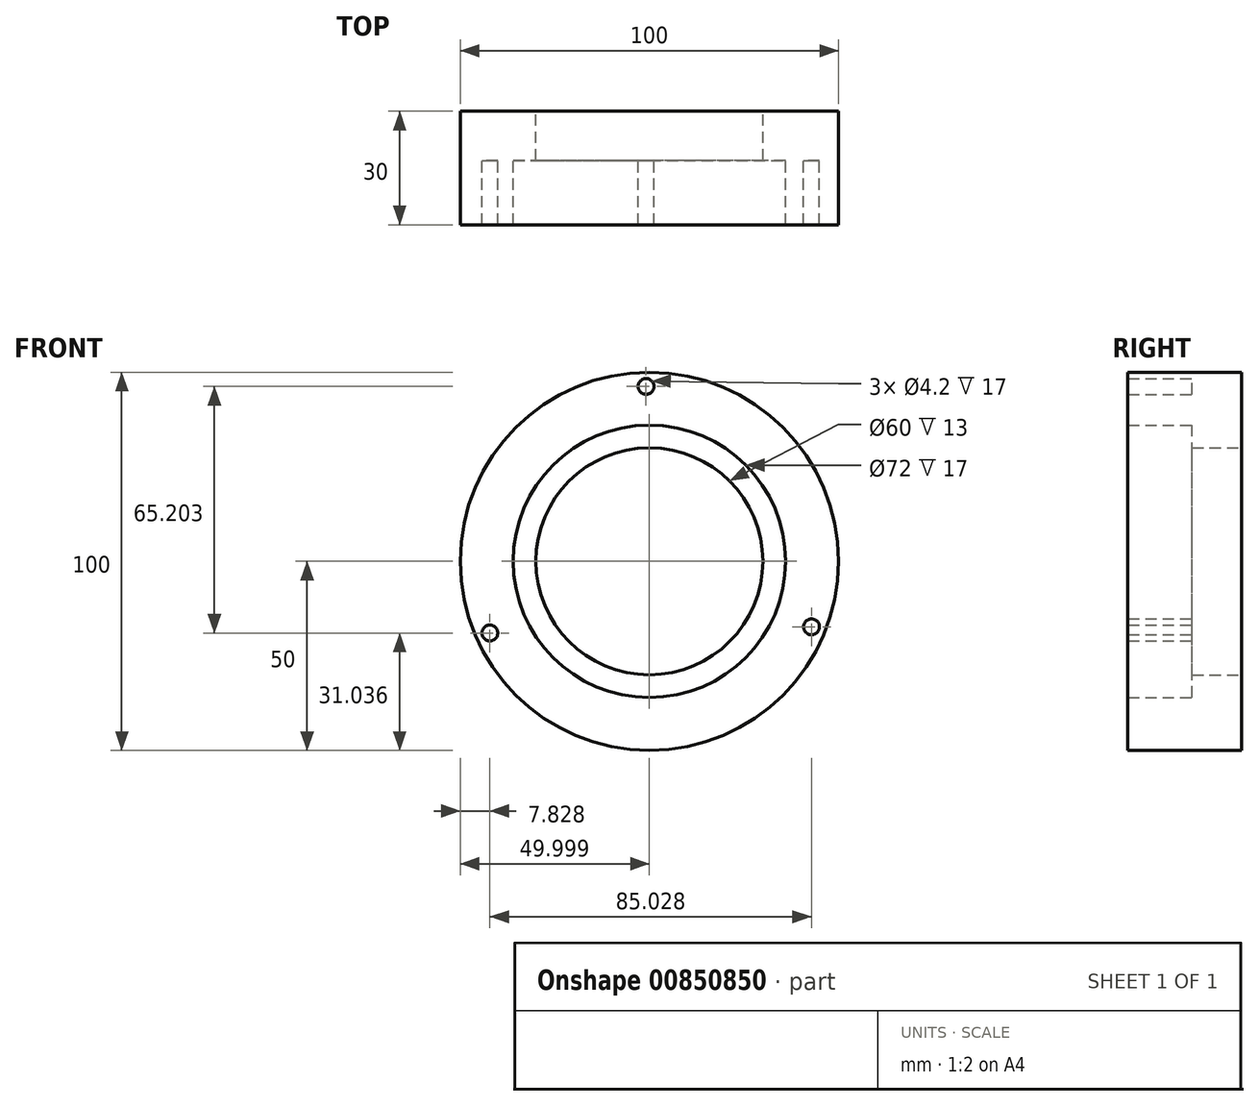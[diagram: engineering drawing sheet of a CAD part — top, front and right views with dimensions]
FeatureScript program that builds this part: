
annotation { "Feature Type Name" : "Feature", "Feature Type Description" : "" }
export const myFeature = defineFeature(function(context is Context, id is Id, definition is map)
    precondition{}
    {
        {
            var Q0;
            Q0=qCreatedBy(makeId("Front.planeOp"),FACE);
            var sketch = newSketch(context, id + "F0", { "sketchPlane" : qUnion([Q0])});
            skCircle(sketch, "E0", {"center": v(-81.37, 0) * mm, "radius": 36 * mm});
            skCircle(sketch, "E1", {"center": v(-81.37, 0) * mm, "radius": 30 * mm});
            skCircle(sketch, "E2", {"center": v(-81.37, 0) * mm, "radius": 50 * mm});
            skCircle(sketch, "E3", {"center": v(-82.27, 46.24) * mm, "radius": 2.1 * mm});
            skCircle(sketch, "E4", {"center": v(-123.54, -18.96) * mm, "radius": 2.1 * mm});
            skCircle(sketch, "E5", {"center": v(-38.51, -17.33) * mm, "radius": 2.1 * mm});
            skSolve(sketch);
        }
        {
            var Q0;
            Q0=makeQuery(id+"F0.imprint","IMPRINT",FACE,{"disambiguationData":[TD([[makeQuery(id+"F0.imprint","IMPRINT",EDGE,{"derivedFrom":sQuery(id+"F0.wireOp",EDGE,"E0")}),1.0]])]});
            extrude(context, id + "F1", {"entities" : qUnion([Q0]), "depth" : 13 * mm, "offsetDistance" : 25.4 * mm});
        }
        {
            var Q0;
            Q0=makeQuery(id+"F0.imprint","IMPRINT",FACE,{"disambiguationData":[TD([[makeQuery(id+"F0.imprint","IMPRINT",EDGE,{"derivedFrom":sQuery(id+"F0.wireOp",EDGE,"E0")}),-1.0]])]});
            extrude(context, id + "F2", {"entities" : qUnion([Q0]), "operationType" : NewBodyOperationType.ADD, "depth" : 30 * mm, "offsetDistance" : 25.4 * mm});
        }
        {
            var Q0;
            Q0=makeQuery(id+"F0.imprint","IMPRINT",FACE,{"disambiguationData":[TD([[makeQuery(id+"F0.imprint","IMPRINT",EDGE,{"derivedFrom":sQuery(id+"F0.wireOp",EDGE,"E4")}),1.0]])]});
            var Q1;
            Q1=makeQuery(id+"F0.imprint","IMPRINT",FACE,{"disambiguationData":[TD([[makeQuery(id+"F0.imprint","IMPRINT",EDGE,{"derivedFrom":sQuery(id+"F0.wireOp",EDGE,"E3")}),1.0]])]});
            var Q2;
            Q2=makeQuery(id+"F0.imprint","IMPRINT",FACE,{"disambiguationData":[TD([[makeQuery(id+"F0.imprint","IMPRINT",EDGE,{"derivedFrom":sQuery(id+"F0.wireOp",EDGE,"E5")}),1.0]])]});
            extrude(context, id + "F3", {"entities" : qUnion([Q0, Q1, Q2]), "operationType" : NewBodyOperationType.ADD, "depth" : 13 * mm, "offsetDistance" : 25.4 * mm});
        }
    });
